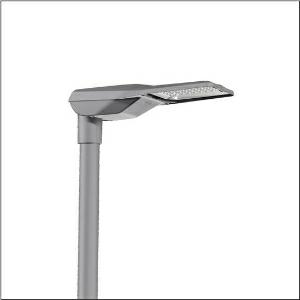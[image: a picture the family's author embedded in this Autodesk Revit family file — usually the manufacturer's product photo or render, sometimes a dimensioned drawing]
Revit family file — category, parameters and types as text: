
# Revit family: streetlight_sl_21_iq_mini___st0_5a_5xe2b31g08jb_3c5a
name_source: partatom
category: Lighting Fixtures
units: mm (PartAtom-declared; Revit-internal decimal feet)

## family parameters
Cut with Voids When Loaded = No
Host = Face
Light Source = No
Part Type = Normal
Room Calculation Point = No
Round Connector Dimension = Use Diameter
Shared = No

## types (1)
- --- (1 x LED, 10820 lm, 71.6 W, 3000K)
    Apparent Load = 72 VA
    CIE Flux Codes = 43 76 97 100 100
    Color Rendering = 70
    Color Temperature = 3000K
    Default Elevation = 1800 mm
    Description = Streetlight SL 21 iQ mini, mast luminaire, primary light control with lens, of PMMA, primary optical cover: cover, of toughened safety glass, transparent, light distribution: ST0.5a, light emission: direct distribution, primary light characteristic: asymmetric, installation type: post-top, side-entry, LED, High Power LED, rated luminous flux: 10.820lm, luminous efficacy: 151lm/W, light colour: 730, colour temperature: 3000K, control gear: iQ Street-Remote, control: Street-Remote, Auto-Match, Temp-Guard, Lumen-Switch, Night-Set, Smart-Wire, Light-Fading, Desk-Remote (wireless, voltage-free reading and setting of iQ features in the workshop via application-optimized NFC function/RFID function), optimised constant luminous flux control (CLO 2.0), pre-setting: linear dimming characteristic, mains connection: 220..240V, AC, 50/60Hz, start of lifetime: 72W, end of service life: 75W, reduction: 33W, luminaire housing, of diecast aluminium, powder-coated, Siteco® metallic grey (DB 702S), corrosivity category C5 mid according to DIN EN ISO 12944, please order mast flange separately, inclination adjustable: 0°, 5°, 10°, 15°, sealing non-destructively replaceable, multi-level sealing system, length: 628mm, width: 235mm, height: 110mm, mast flange for spigot size: 42mm (side-entry): 5XC10008XM4, 60/48mm (side-entry/post-top): 5XC10108XM2, 76/60mm (side-entry/post-top): 5XC10108XM1, mounting height: 4..8m, protection rating (complete): IP66, insulation class (complete): insulation class II (safety insulation), certification: CE, ENEC, ENEC+, VDE, impact resistance: IK10, permissible operating ambient temperature for outdoor applications: -40..+50°C, standard-compliant lighting for roads and squares, packaging unit: 1 piece

Light Distribution: ST0.5a
    Height = 110 mm
    Lamp = 1 x LED
    Lamp Light Flux = 10820 lm
    Lamp Power = 71.6 W
    Lamp count = 1
    Length = 625 mm
    Luminous efficacy = 151 lm/W
    Manufacturer = Siteco
    ModVariant = No
    Model = 5XE2B31G08JB
    Number of Poles = 1
    OnlyDefault = Yes
    Power Factor = 1
    Product Name = Streetlight SL 21 iQ mini | ST0.5a
    Product group = mast luminaire | pylon top
    ProductGroupID = 6100
    Protection Class = Protection class II
    Protection Degree = IP 66
    RLX_Detail_Level = 1
    RLX_Emergency_Light_Flux = 0 lm
    RLX_Emergency_Type = 0
    RLX_Emergency_Type_DB = No
    RlxData = <blob elided: 37545 chars, md5=bd0a7ce2>
    Socket = socket
    Standby Power = 0 W
    System Light Flux = 10820 lm
    System Power = 72 W
    Type Comments = factory setting: luminous flux: 100 % | dim-lin: 254 | 746 mA
    Type Image = l_1003519.jpg
    URL = http://relux.com
    VarID = @adj_171778
    Voltage = 0 V
    Weight = 0.00 kg
    Width = 234 mm

## geometry (parser evidence)
native form markers: Blend x4, Sweep x11
no freeform markers — native parametric forms only
